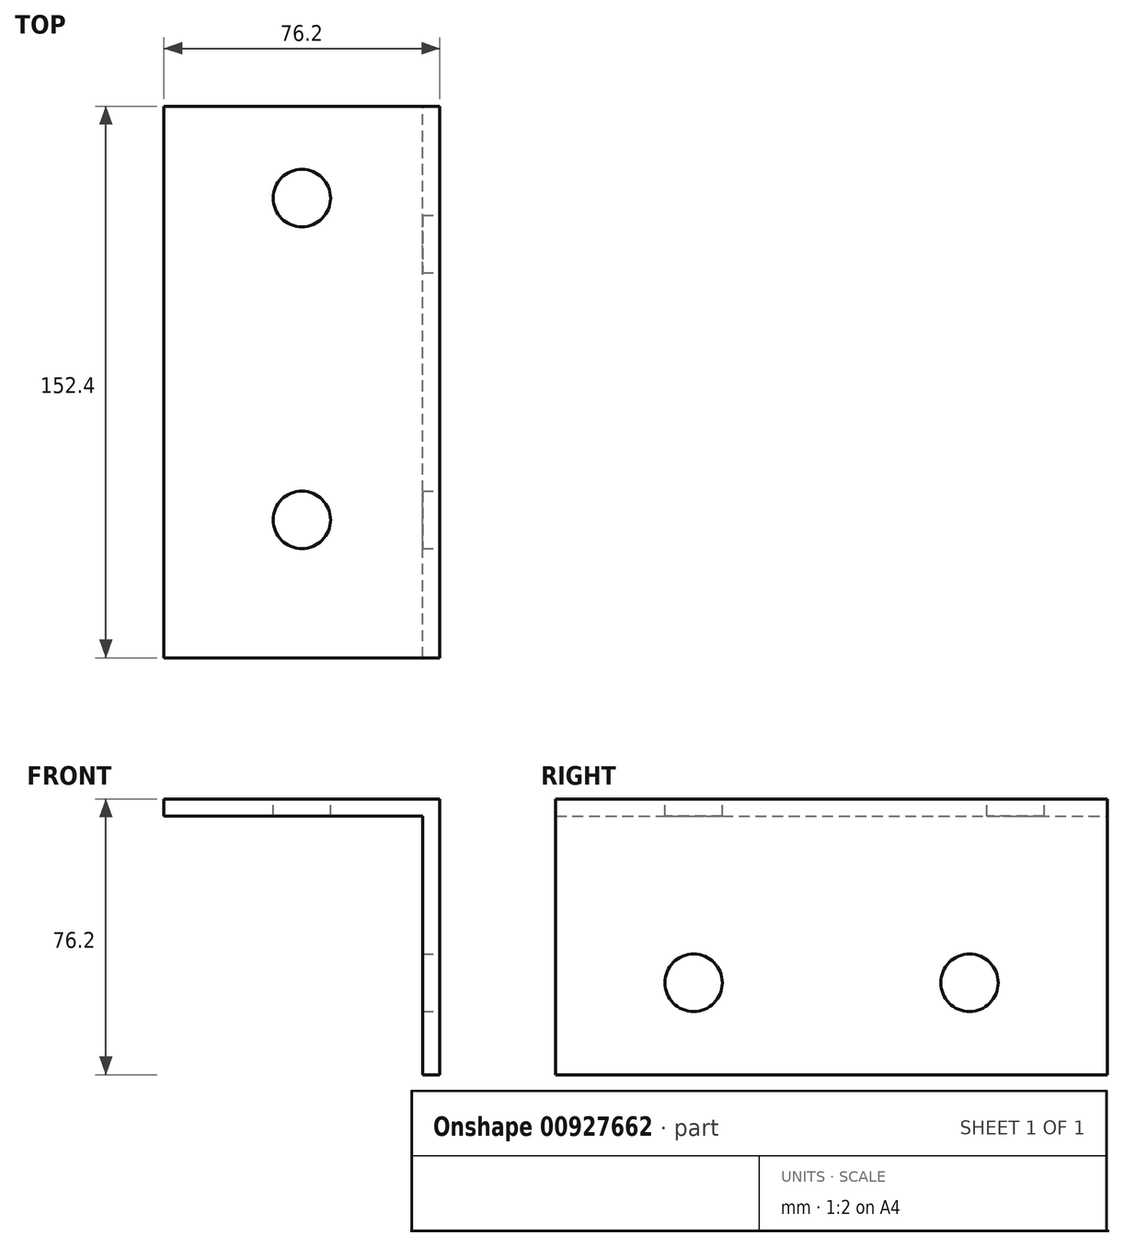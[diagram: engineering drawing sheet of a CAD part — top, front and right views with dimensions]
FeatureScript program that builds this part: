
annotation { "Feature Type Name" : "Feature", "Feature Type Description" : "" }
export const myFeature = defineFeature(function(context is Context, id is Id, definition is map)
    precondition{}
    {
        {
            var Q0;
            Q0=qCreatedBy(makeId("Right.planeOp"),FACE);
            var sketch = newSketch(context, id + "F0", { "sketchPlane" : qUnion([Q0])});
            skLineSegment(sketch, "E0.bottom", {"start": v(76.2, 45.57) * mm, "end": v(-76.2, 45.57) * mm});
            skLineSegment(sketch, "E0.top", {"start": v(76.2, -30.63) * mm, "end": v(-76.2, -30.63) * mm});
            skLineSegment(sketch, "E0.left", {"start": v(76.2, 45.57) * mm, "end": v(76.2, -30.63) * mm});
            skLineSegment(sketch, "E0.right", {"start": v(-76.2, 45.57) * mm, "end": v(-76.2, -30.63) * mm});
            skPoint(sketch, "E0.middle", {"position": v(0, 7.47) * mm});
            skSolve(sketch);
        }
        {
            var Q0;
            Q0 = qSketchRegion(id + "F0", true);
            extrude(context, id + "F1", {"entities" : qUnion([Q0]), "oppositeDirection" : true, "depth" : 76.2 * mm, "offsetDistance" : 25.4 * mm});
        }
        {
            var Q0;
            Q0=makeQuery(id+"F1.opExtrude","SWEPT_FACE",FACE,{"disambiguationData":[OSD([sQuery(id+"F0.wireOp",EDGE,"E0.left")])]});
            var sketch = newSketch(context, id + "F2", { "sketchPlane" : qUnion([Q0])});
            skLineSegment(sketch, "E1.0", {"start": v(4.76, 40.81) * mm, "end": v(4.76, -30.63) * mm});
            skLineSegment(sketch, "E1.1", {"start": v(76.2, 40.81) * mm, "end": v(4.76, 40.81) * mm});
            skLineSegment(sketch, "E2", {"start": v(4.76, -30.63) * mm, "end": v(76.2, -30.63) * mm});
            skLineSegment(sketch, "E3", {"start": v(76.2, -30.63) * mm, "end": v(76.2, 40.81) * mm});
            skSolve(sketch);
        }
        {
            var Q0;
            Q0 = qSketchRegion(id + "F2", true);
            extrude(context, id + "F3", {"entities" : qUnion([Q0]), "operationType" : NewBodyOperationType.REMOVE, "oppositeDirection" : true, "depth" : 152.4 * mm, "offsetDistance" : 25.4 * mm});
        }
        {
            var Q0;
            Q0=makeQuery(id+"F1.opExtrude","CAP_FACE",FACE,{"disambiguationData":[OSD([sQuery(id+"F0.wireOp",EDGE,"E0.bottom"),sQuery(id+"F0.wireOp",EDGE,"E0.top"),sQuery(id+"F0.wireOp",EDGE,"E0.left"),sQuery(id+"F0.wireOp",EDGE,"E0.right")])],"isStart":true});
            var sketch = newSketch(context, id + "F4", { "sketchPlane" : qUnion([Q0])});
            skCircle(sketch, "E4", {"center": v(-38.1, -5.23) * mm, "radius": 7.94 * mm});
            skCircle(sketch, "E5", {"center": v(38.1, -5.23) * mm, "radius": 7.94 * mm});
            skSolve(sketch);
        }
        {
            var Q0;
            Q0 = qSketchRegion(id + "F4", true);
            extrude(context, id + "F5", {"entities" : qUnion([Q0]), "operationType" : NewBodyOperationType.REMOVE, "endBound" : BoundingType.UP_TO_NEXT, "oppositeDirection" : true, "depth" : 25.4 * mm, "offsetDistance" : 25.4 * mm});
        }
        {
            var Q0;
            Q0=makeQuery(id+"F1.opExtrude","SWEPT_FACE",FACE,{"disambiguationData":[OSD([sQuery(id+"F0.wireOp",EDGE,"E0.bottom")])]});
            var sketch = newSketch(context, id + "F6", { "sketchPlane" : qUnion([Q0])});
            skCircle(sketch, "E6", {"center": v(-38.1, 50.8) * mm, "radius": 7.94 * mm});
            skCircle(sketch, "E7", {"center": v(-38.1, -38.1) * mm, "radius": 7.94 * mm});
            skSolve(sketch);
        }
        {
            var Q0;
            Q0 = qSketchRegion(id + "F6", true);
            extrude(context, id + "F7", {"entities" : qUnion([Q0]), "operationType" : NewBodyOperationType.REMOVE, "endBound" : BoundingType.UP_TO_NEXT, "oppositeDirection" : true, "depth" : 25.4 * mm, "offsetDistance" : 25.4 * mm});
        }
    });
